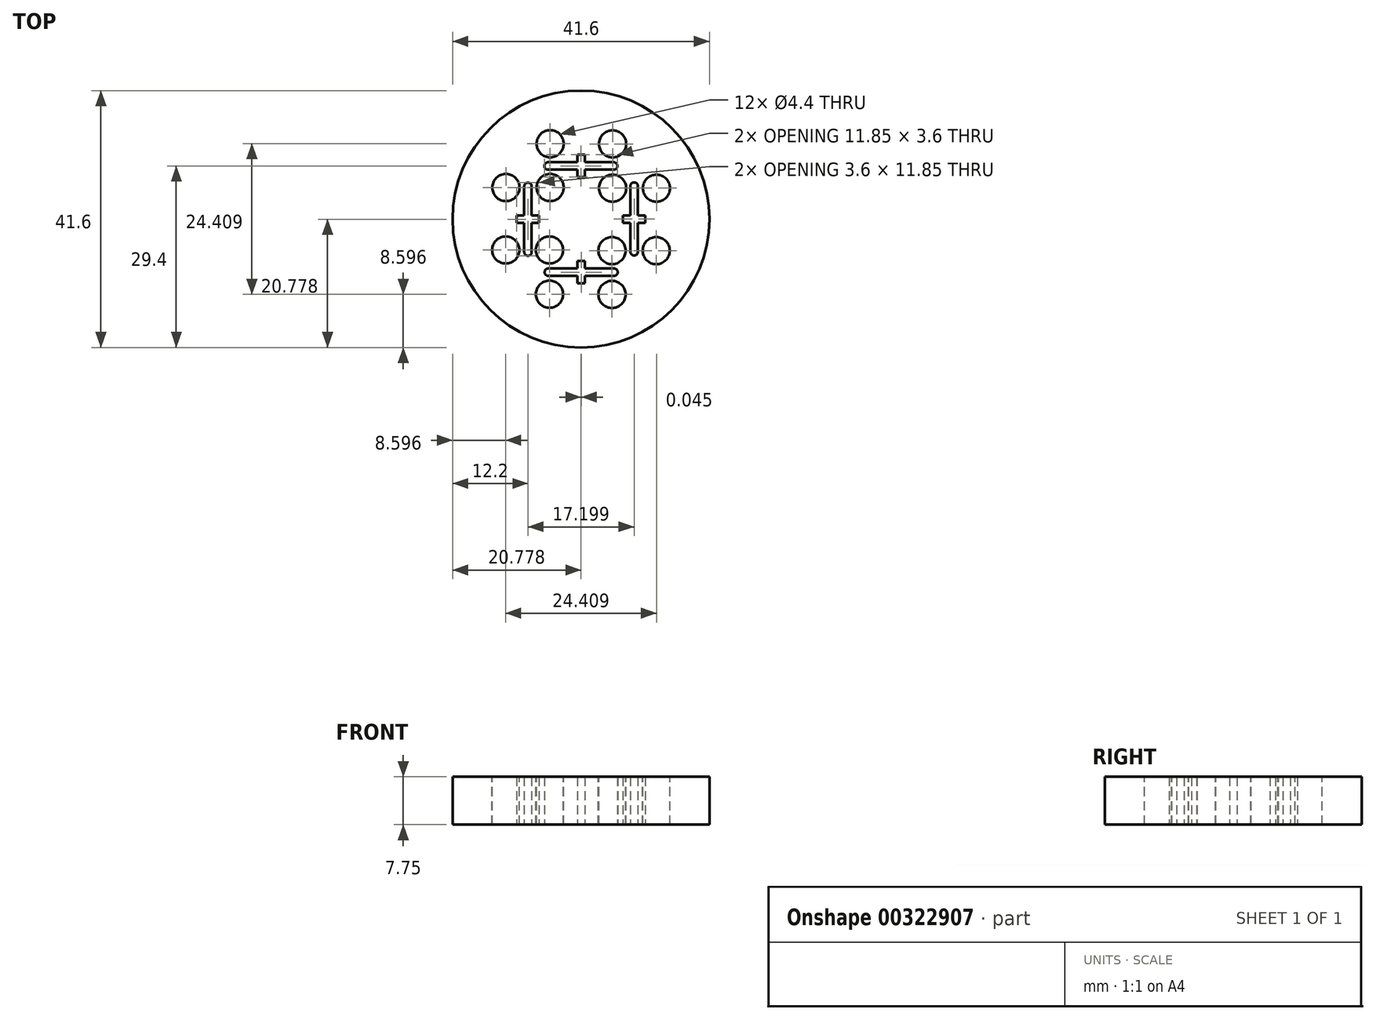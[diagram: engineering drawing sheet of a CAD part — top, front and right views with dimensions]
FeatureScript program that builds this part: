
annotation { "Feature Type Name" : "Feature", "Feature Type Description" : "" }
export const myFeature = defineFeature(function(context is Context, id is Id, definition is map)
    precondition{}
    {
        {
            var Q0;
            Q0=qCreatedBy(makeId("Top.planeOp"),FACE);
            var sketch = newSketch(context, id + "F0", { "sketchPlane" : qUnion([Q0])});
            skCircle(sketch, "E0", {"center": v(0, 0) * mm, "radius": 20.8 * mm});
            skSolve(sketch);
        }
        {
            var Q0;
            Q0 = qSketchRegion(id + "F0", true);
            extrude(context, id + "F1", {"entities" : qUnion([Q0]), "depth" : 7.75 * mm});
        }
        {
            var Q0;
            Q0=makeQuery(id+"F1.opExtrude","CAP_FACE",FACE,{"disambiguationData":[OSD([sQuery(id+"F0.wireOp",EDGE,"E0")])],"isStart":false});
            var sketch = newSketch(context, id + "F2", { "sketchPlane" : qUnion([Q0])});
            skCircle(sketch, "E1", {"center": v(-5, 12.2) * mm, "radius": 2.2 * mm});
            skCircle(sketch, "E2", {"center": v(-5, 5.1) * mm, "radius": 2.2 * mm});
            skCircle(sketch, "E3", {"center": v(-12.17, 5.1) * mm, "radius": 2.2 * mm});
            skCircle(sketch, "E4.1.0", {"center": v(-12.2, -5) * mm, "radius": 2.2 * mm});
            skCircle(sketch, "E4.1.1", {"center": v(-5.1, -5) * mm, "radius": 2.2 * mm});
            skCircle(sketch, "E4.1.2", {"center": v(-5.1, -12.17) * mm, "radius": 2.2 * mm});
            skCircle(sketch, "E4.2.0", {"center": v(5, -12.2) * mm, "radius": 2.2 * mm});
            skCircle(sketch, "E4.2.1", {"center": v(5, -5.1) * mm, "radius": 2.2 * mm});
            skCircle(sketch, "E4.2.2", {"center": v(12.17, -5.1) * mm, "radius": 2.2 * mm});
            skCircle(sketch, "E4.3.0", {"center": v(12.2, 5) * mm, "radius": 2.2 * mm});
            skCircle(sketch, "E4.3.1", {"center": v(5.1, 5) * mm, "radius": 2.2 * mm});
            skCircle(sketch, "E4.3.2", {"center": v(5.1, 12.17) * mm, "radius": 2.2 * mm});
            skPoint(sketch, "E4.center", {"position": v(0, 0) * mm});
            skSolve(sketch);
        }
        {
            var Q0;
            Q0 = qSketchRegion(id + "F2", true);
            extrude(context, id + "F3", {"entities" : qUnion([Q0]), "operationType" : NewBodyOperationType.REMOVE, "endBound" : BoundingType.THROUGH_ALL, "oppositeDirection" : true, "depth" : 25 * mm});
        }
        {
            var Q0;
            Q0=makeQuery(id+"F1.opExtrude","CAP_FACE",FACE,{"disambiguationData":[OSD([sQuery(id+"F0.wireOp",EDGE,"E0")])],"isStart":true});
            var sketch = newSketch(context, id + "F4", { "sketchPlane" : qUnion([Q0])});
            skLineSegment(sketch, "E5", {"start": v(6.8, -0.6) * mm, "end": v(6.8, 0.6) * mm});
            skLineSegment(sketch, "E6", {"start": v(10.4, -0.6) * mm, "end": v(10.4, 0.6) * mm});
            skLineSegment(sketch, "E7", {"start": v(10.4, -0.6) * mm, "end": v(9.2, -0.6) * mm});
            skLineSegment(sketch, "E8", {"start": v(6.8, -0.6) * mm, "end": v(8, -0.6) * mm});
            skLineSegment(sketch, "E9", {"start": v(9.2, -1.8) * mm, "end": v(9.2, -0.6) * mm});
            skLineSegment(sketch, "E10", {"start": v(6.8, 0.6) * mm, "end": v(8, 0.6) * mm});
            skLineSegment(sketch, "E11", {"start": v(8, 0.6) * mm, "end": v(8, 1.8) * mm});
            skLineSegment(sketch, "E12", {"start": v(9.2, 1.8) * mm, "end": v(9.2, 0.6) * mm});
            skLineSegment(sketch, "E13", {"start": v(9.2, 0.6) * mm, "end": v(10.4, 0.6) * mm});
            skLineSegment(sketch, "E14", {"start": v(9.2, -1.8) * mm, "end": v(9.2, -5.34) * mm});
            skLineSegment(sketch, "E15", {"start": v(9.2, 1.8) * mm, "end": v(9.2, 5.3) * mm});
            skLineSegment(sketch, "E16", {"start": v(8, 1.8) * mm, "end": v(8, 5.3) * mm});
            skArc(sketch, "E17", {"start": v(8, -5.34) * mm, "mid": v(8.6, -5.95) * mm, "end": v(9.2, -5.34) * mm});
            skArc(sketch, "E18", {"start": v(9.2, 5.3) * mm, "mid": v(8.6, 5.9) * mm, "end": v(8, 5.3) * mm});
            skLineSegment(sketch, "E19", {"start": v(8, -0.6) * mm, "end": v(8, -1.8) * mm});
            skLineSegment(sketch, "E20", {"start": v(8, -5.34) * mm, "end": v(8, -1.8) * mm});
            skArc(sketch, "E21.1.0", {"start": v(-5.3, 9.2) * mm, "mid": v(-5.9, 8.6) * mm, "end": v(-5.3, 8) * mm});
            skLineSegment(sketch, "E21.1.1", {"start": v(0.6, 8) * mm, "end": v(1.8, 8) * mm});
            skLineSegment(sketch, "E21.1.2", {"start": v(-0.6, 9.2) * mm, "end": v(-0.6, 10.4) * mm});
            skLineSegment(sketch, "E21.1.3", {"start": v(0.6, 10.4) * mm, "end": v(0.6, 9.2) * mm});
            skLineSegment(sketch, "E21.1.4", {"start": v(1.8, 9.2) * mm, "end": v(0.6, 9.2) * mm});
            skLineSegment(sketch, "E21.1.5", {"start": v(1.8, 9.2) * mm, "end": v(5.34, 9.2) * mm});
            skLineSegment(sketch, "E21.1.6", {"start": v(-1.8, 9.2) * mm, "end": v(-5.3, 9.2) * mm});
            skLineSegment(sketch, "E21.1.7", {"start": v(-1.8, 8) * mm, "end": v(-5.3, 8) * mm});
            skArc(sketch, "E21.1.8", {"start": v(5.34, 8) * mm, "mid": v(5.95, 8.6) * mm, "end": v(5.34, 9.2) * mm});
            skLineSegment(sketch, "E21.1.9", {"start": v(5.34, 8) * mm, "end": v(1.8, 8) * mm});
            skLineSegment(sketch, "E21.1.10", {"start": v(0.6, 6.8) * mm, "end": v(-0.6, 6.8) * mm});
            skLineSegment(sketch, "E21.1.11", {"start": v(0.6, 10.4) * mm, "end": v(-0.6, 10.4) * mm});
            skLineSegment(sketch, "E21.1.12", {"start": v(0.6, 6.8) * mm, "end": v(0.6, 8) * mm});
            skLineSegment(sketch, "E21.1.13", {"start": v(-0.6, 6.8) * mm, "end": v(-0.6, 8) * mm});
            skLineSegment(sketch, "E21.1.14", {"start": v(-0.6, 8) * mm, "end": v(-1.8, 8) * mm});
            skLineSegment(sketch, "E21.1.15", {"start": v(-1.8, 9.2) * mm, "end": v(-0.6, 9.2) * mm});
            skArc(sketch, "E21.2.0", {"start": v(-9.2, -5.3) * mm, "mid": v(-8.6, -5.9) * mm, "end": v(-8, -5.3) * mm});
            skLineSegment(sketch, "E21.2.1", {"start": v(-8, 0.6) * mm, "end": v(-8, 1.8) * mm});
            skLineSegment(sketch, "E21.2.2", {"start": v(-9.2, -0.6) * mm, "end": v(-10.4, -0.6) * mm});
            skLineSegment(sketch, "E21.2.3", {"start": v(-10.4, 0.6) * mm, "end": v(-9.2, 0.6) * mm});
            skLineSegment(sketch, "E21.2.4", {"start": v(-9.2, 1.8) * mm, "end": v(-9.2, 0.6) * mm});
            skLineSegment(sketch, "E21.2.5", {"start": v(-9.2, 1.8) * mm, "end": v(-9.2, 5.34) * mm});
            skLineSegment(sketch, "E21.2.6", {"start": v(-9.2, -1.8) * mm, "end": v(-9.2, -5.3) * mm});
            skLineSegment(sketch, "E21.2.7", {"start": v(-8, -1.8) * mm, "end": v(-8, -5.3) * mm});
            skArc(sketch, "E21.2.8", {"start": v(-8, 5.34) * mm, "mid": v(-8.6, 5.95) * mm, "end": v(-9.2, 5.34) * mm});
            skLineSegment(sketch, "E21.2.9", {"start": v(-8, 5.34) * mm, "end": v(-8, 1.8) * mm});
            skLineSegment(sketch, "E21.2.10", {"start": v(-6.8, 0.6) * mm, "end": v(-6.8, -0.6) * mm});
            skLineSegment(sketch, "E21.2.11", {"start": v(-10.4, 0.6) * mm, "end": v(-10.4, -0.6) * mm});
            skLineSegment(sketch, "E21.2.12", {"start": v(-6.8, 0.6) * mm, "end": v(-8, 0.6) * mm});
            skLineSegment(sketch, "E21.2.13", {"start": v(-6.8, -0.6) * mm, "end": v(-8, -0.6) * mm});
            skLineSegment(sketch, "E21.2.14", {"start": v(-8, -0.6) * mm, "end": v(-8, -1.8) * mm});
            skLineSegment(sketch, "E21.2.15", {"start": v(-9.2, -1.8) * mm, "end": v(-9.2, -0.6) * mm});
            skArc(sketch, "E21.3.0", {"start": v(5.3, -9.2) * mm, "mid": v(5.9, -8.6) * mm, "end": v(5.3, -8) * mm});
            skLineSegment(sketch, "E21.3.1", {"start": v(-0.6, -8) * mm, "end": v(-1.8, -8) * mm});
            skLineSegment(sketch, "E21.3.2", {"start": v(0.6, -9.2) * mm, "end": v(0.6, -10.4) * mm});
            skLineSegment(sketch, "E21.3.3", {"start": v(-0.6, -10.4) * mm, "end": v(-0.6, -9.2) * mm});
            skLineSegment(sketch, "E21.3.4", {"start": v(-1.8, -9.2) * mm, "end": v(-0.6, -9.2) * mm});
            skLineSegment(sketch, "E21.3.5", {"start": v(-1.8, -9.2) * mm, "end": v(-5.34, -9.2) * mm});
            skLineSegment(sketch, "E21.3.6", {"start": v(1.8, -9.2) * mm, "end": v(5.3, -9.2) * mm});
            skLineSegment(sketch, "E21.3.7", {"start": v(1.8, -8) * mm, "end": v(5.3, -8) * mm});
            skArc(sketch, "E21.3.8", {"start": v(-5.34, -8) * mm, "mid": v(-5.95, -8.6) * mm, "end": v(-5.34, -9.2) * mm});
            skLineSegment(sketch, "E21.3.9", {"start": v(-5.34, -8) * mm, "end": v(-1.8, -8) * mm});
            skLineSegment(sketch, "E21.3.10", {"start": v(-0.6, -6.8) * mm, "end": v(0.6, -6.8) * mm});
            skLineSegment(sketch, "E21.3.11", {"start": v(-0.6, -10.4) * mm, "end": v(0.6, -10.4) * mm});
            skLineSegment(sketch, "E21.3.12", {"start": v(-0.6, -6.8) * mm, "end": v(-0.6, -8) * mm});
            skLineSegment(sketch, "E21.3.13", {"start": v(0.6, -6.8) * mm, "end": v(0.6, -8) * mm});
            skLineSegment(sketch, "E21.3.14", {"start": v(0.6, -8) * mm, "end": v(1.8, -8) * mm});
            skLineSegment(sketch, "E21.3.15", {"start": v(1.8, -9.2) * mm, "end": v(0.6, -9.2) * mm});
            skPoint(sketch, "E21.center", {"position": v(0, 0) * mm});
            skSolve(sketch);
        }
        {
            var Q0;
            Q0 = qSketchRegion(id + "F4", true);
            extrude(context, id + "F5", {"entities" : qUnion([Q0]), "operationType" : NewBodyOperationType.REMOVE, "endBound" : BoundingType.THROUGH_ALL, "oppositeDirection" : true, "depth" : 25 * mm});
        }
    });
